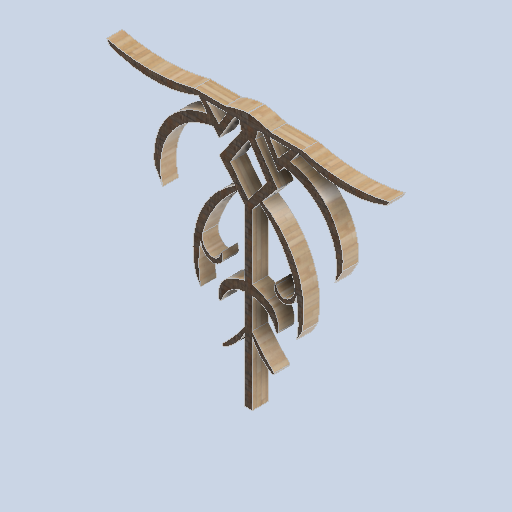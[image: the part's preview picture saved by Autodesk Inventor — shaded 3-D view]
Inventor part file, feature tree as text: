
AUTODESK INVENTOR PART (.ipt)
format: ipt  version: 2024.2 (Build 282272000, 272)  size: 374,784 bytes
history: native  units: in
note: dims shown in document units (in); Inventor stores cm internally (conversion verified against a paired STEP export)
features: sketch x4, other x3, plane x1
ambient origin geometry x8: Origin, YZ Plane, XZ Plane, XY Plane, X Axis, Y Axis, Z Axis, Center Point
bodies: Solid1 (feature_tree)
feature tree (8):
  other  "side_art_frame_01.ipt"
  other  "Solid1::side_art_frame_01.ipt"
  other  "TaggingFeature1"
  sketch  "Sketch1"  dims[d0=0.3937in]
  sketch  "Sketch2"
  sketch  "Sketch3"
  sketch  "Sketch4"
  plane  "Work Plane1"
